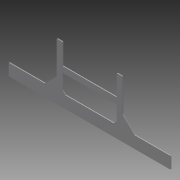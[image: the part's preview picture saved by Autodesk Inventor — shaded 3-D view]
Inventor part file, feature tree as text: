
AUTODESK INVENTOR PART (.ipt)
format: ipt  version: 2014 (Build 180170000, 170)  size: 141,824 bytes
history: native  units: in
note: dims shown in document units (in); Inventor stores cm internally (conversion verified against a paired STEP export)
features: extrude x1
ambient origin geometry x8: Origin, YZ Plane, XZ Plane, XY Plane, X Axis, Y Axis, Z Axis, Center Point
bodies: Solid1 (feature_tree)
feature tree (1):
  extrude  "Extrusion1"  Depth=27.125in
